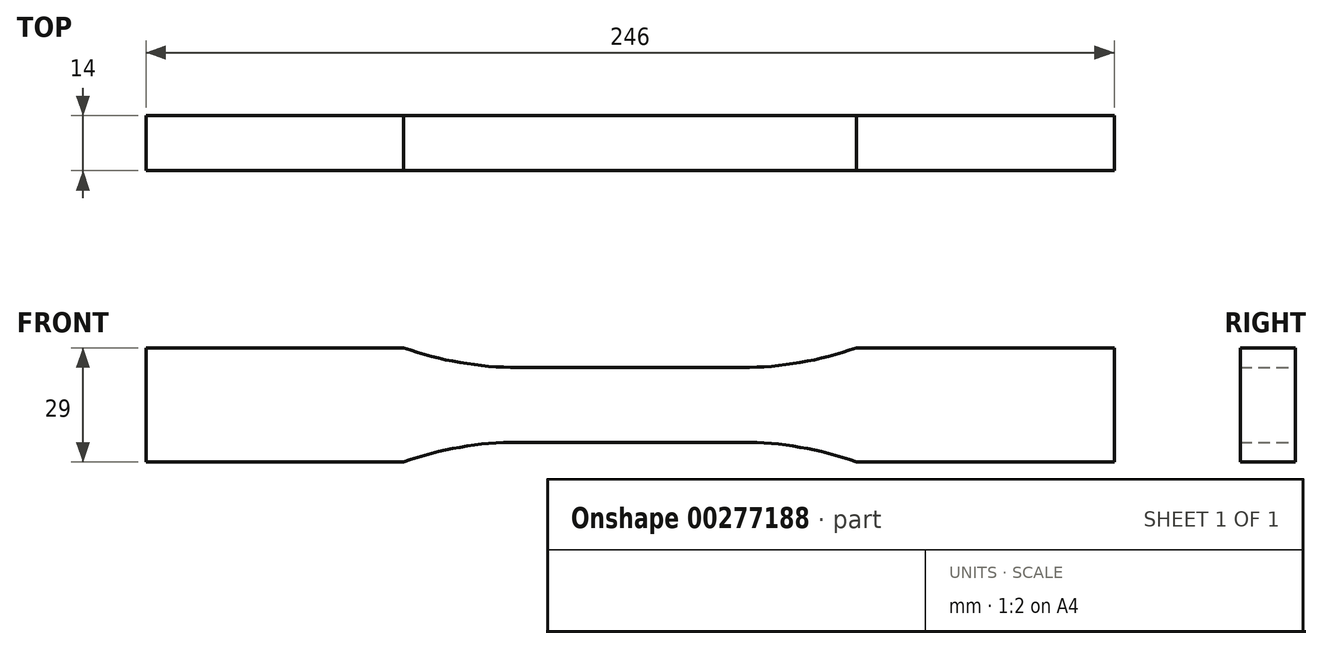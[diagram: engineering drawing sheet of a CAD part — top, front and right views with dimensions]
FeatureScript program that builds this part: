
annotation { "Feature Type Name" : "Feature", "Feature Type Description" : "" }
export const myFeature = defineFeature(function(context is Context, id is Id, definition is map)
    precondition{}
    {
        {
            var Q0;
            Q0=qCreatedBy(makeId("Front.planeOp"),FACE);
            var sketch = newSketch(context, id + "F0", { "sketchPlane" : qUnion([Q0])});
            skLineSegment(sketch, "E0", {"start": v(0, 9.5) * mm, "end": v(28.5, 9.5) * mm});
            skArc(sketch, "E1", {"start": v(28.5, 9.5) * mm, "mid": v(43.21, 10.76) * mm, "end": v(57.5, 14.5) * mm});
            skLineSegment(sketch, "E2", {"start": v(57.5, 14.5) * mm, "end": v(123, 14.5) * mm});
            skLineSegment(sketch, "E3", {"start": v(123, 14.5) * mm, "end": v(123, 0) * mm});
            skLineSegment(sketch, "E4.MirrorCS", {"start": v(0, -9.5) * mm, "end": v(28.5, -9.5) * mm});
            skLineSegment(sketch, "E5.MirrorCS", {"start": v(123, -14.5) * mm, "end": v(123, 0) * mm});
            skLineSegment(sketch, "E6.MirrorCS", {"start": v(57.5, -14.5) * mm, "end": v(123, -14.5) * mm});
            skArc(sketch, "E7.MirrorCS", {"start": v(28.5, -9.5) * mm, "mid": v(43.21, -10.76) * mm, "end": v(57.5, -14.5) * mm});
            skArc(sketch, "E8.MirrorCS", {"start": v(-28.5, -9.5) * mm, "mid": v(-43.21, -10.76) * mm, "end": v(-57.5, -14.5) * mm});
            skLineSegment(sketch, "E9.MirrorCS", {"start": v(-57.5, -14.5) * mm, "end": v(-123, -14.5) * mm});
            skLineSegment(sketch, "E10.MirrorCS", {"start": v(0, 9.5) * mm, "end": v(-28.5, 9.5) * mm});
            skArc(sketch, "E11.MirrorCS", {"start": v(-28.5, 9.5) * mm, "mid": v(-43.21, 10.76) * mm, "end": v(-57.5, 14.5) * mm});
            skLineSegment(sketch, "E12.MirrorCS", {"start": v(-57.5, 14.5) * mm, "end": v(-123, 14.5) * mm});
            skLineSegment(sketch, "E13.MirrorCS", {"start": v(-123, -14.5) * mm, "end": v(-123, 0) * mm});
            skLineSegment(sketch, "E14.MirrorCS", {"start": v(-123, 14.5) * mm, "end": v(-123, 0) * mm});
            skLineSegment(sketch, "E15.MirrorCS", {"start": v(0, -9.5) * mm, "end": v(-28.5, -9.5) * mm});
            skSolve(sketch);
        }
        {
            var Q0;
            Q0=makeQuery(id+"F0.imprint","IMPRINT",FACE,{"disambiguationData":[TD([[makeQuery(id+"F0.imprint","IMPRINT",EDGE,{"derivedFrom":sQuery(id+"F0.wireOp",EDGE,"E1")}),-1.0]])]});
            extrude(context, id + "F1", {"entities" : qUnion([Q0]), "endBound" : BoundingType.SYMMETRIC, "depth" : 14 * mm});
        }
    });
